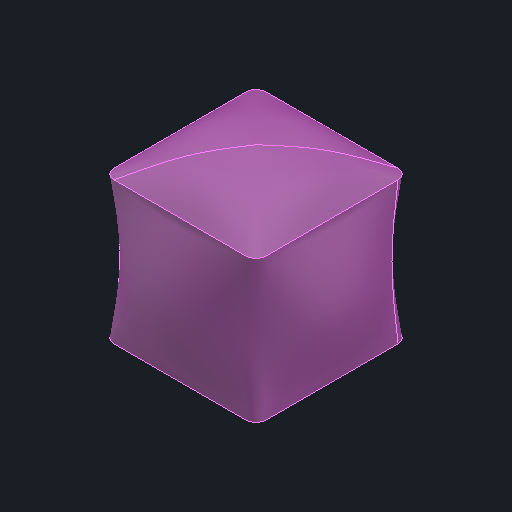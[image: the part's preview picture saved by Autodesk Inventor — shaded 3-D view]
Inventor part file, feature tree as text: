
AUTODESK INVENTOR PART (.ipt)
format: ipt  version: 2023 (Build 270158000, 158)  size: 311,296 bytes
history: native  units: in
note: dims shown in document units (in); Inventor stores cm internally (conversion verified against a paired STEP export)
features: loft x1
ambient origin geometry x8: Origin, YZ Plane, XZ Plane, XY Plane, X Axis, Y Axis, Z Axis, Center Point
bodies: Solid1 (feature_tree)
feature tree (1):
  loft  "Loft6"
